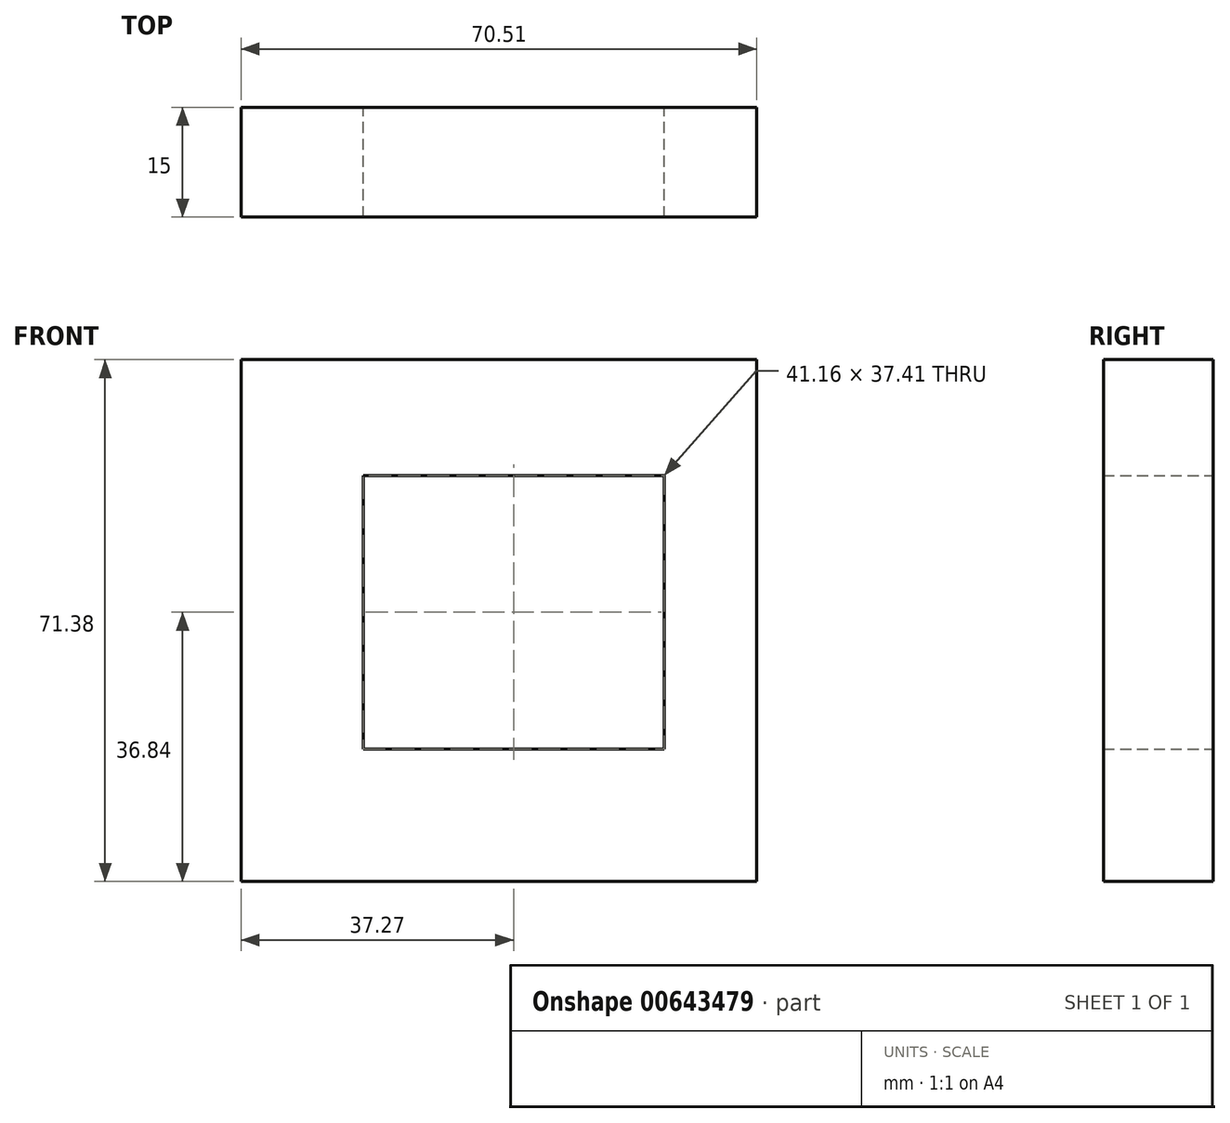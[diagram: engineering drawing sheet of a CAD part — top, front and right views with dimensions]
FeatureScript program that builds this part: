
annotation { "Feature Type Name" : "Feature", "Feature Type Description" : "" }
export const myFeature = defineFeature(function(context is Context, id is Id, definition is map)
    precondition{}
    {
        {
            var Q0;
            Q0=qCreatedBy(makeId("Front.planeOp"),FACE);
            var sketch = newSketch(context, id + "F0", { "sketchPlane" : qUnion([Q0])});
            skLineSegment(sketch, "E0", {"start": v(-63.46, -24.32) * mm, "end": v(7.05, -24.32) * mm});
            skLineSegment(sketch, "E1", {"start": v(7.05, -24.32) * mm, "end": v(7.05, 47.06) * mm});
            skLineSegment(sketch, "E2", {"start": v(7.05, 47.06) * mm, "end": v(-63.46, 47.06) * mm});
            skPoint(sketch, "E3.start.orphan", {"position": v(-63.46, 45.62) * mm});
            skLineSegment(sketch, "E4", {"start": v(-63.46, 47.06) * mm, "end": v(-63.46, -24.32) * mm});
            skLineSegment(sketch, "E5.bottom", {"start": v(-46.77, 31.23) * mm, "end": v(-5.61, 31.23) * mm});
            skLineSegment(sketch, "E5.top", {"start": v(-46.77, -6.19) * mm, "end": v(-5.61, -6.19) * mm});
            skLineSegment(sketch, "E5.left", {"start": v(-46.77, 31.23) * mm, "end": v(-46.77, -6.19) * mm});
            skLineSegment(sketch, "E5.right", {"start": v(-5.61, 31.23) * mm, "end": v(-5.61, -6.19) * mm});
            skSolve(sketch);
        }
        {
            var Q0;
            Q0 = qSketchRegion(id + "F0", true);
            extrude(context, id + "F1", {"entities" : qUnion([Q0]), "depth" : 15 * mm, "offsetDistance" : 25 * mm});
        }
    });
